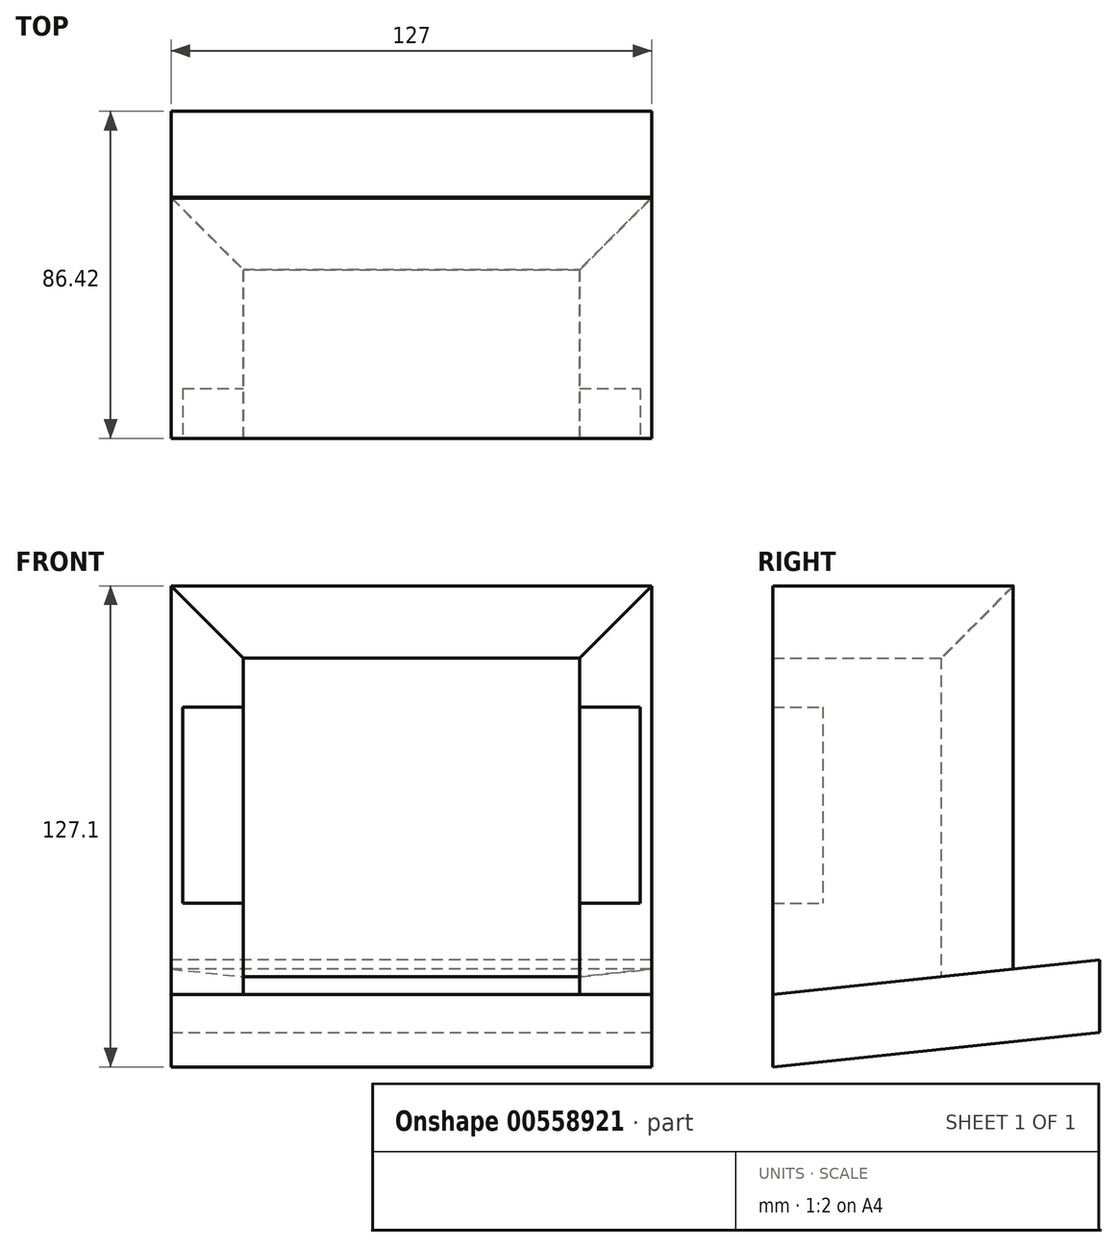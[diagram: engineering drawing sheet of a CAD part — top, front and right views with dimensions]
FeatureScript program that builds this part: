
annotation { "Feature Type Name" : "Feature", "Feature Type Description" : "" }
export const myFeature = defineFeature(function(context is Context, id is Id, definition is map)
    precondition{}
    {
        {
            var Q0;
            Q0=qCreatedBy(makeId("Right.planeOp"),FACE);
            cPlane(context, id + "F0", {"entities" : qUnion([Q0]), "cplaneType" : CPlaneType.OFFSET, "offset" : 63.5 * mm, "oppositeDirection" : true, "width" : 152.4 * mm, "height" : 152.4 * mm});
        }
        {
            var Q0;
            Q0=qCreatedBy(makeId("Right.planeOp"),FACE);
            cPlane(context, id + "F1", {"entities" : qUnion([Q0]), "cplaneType" : CPlaneType.OFFSET, "offset" : 63.5 * mm, "width" : 152.4 * mm, "height" : 152.4 * mm});
        }
        {
            var Q0;
            Q0=qCreatedBy(makeId("Top.planeOp"),FACE);
            cPlane(context, id + "F2", {"entities" : qUnion([Q0]), "cplaneType" : CPlaneType.OFFSET, "offset" : 63.5 * mm, "width" : 152.4 * mm, "height" : 152.4 * mm});
        }
        {
            var Q0;
            Q0=qCreatedBy(makeId("Front.planeOp"),FACE);
            cPlane(context, id + "F3", {"entities" : qUnion([Q0]), "cplaneType" : CPlaneType.OFFSET, "offset" : 63.5 * mm, "width" : 152.4 * mm, "height" : 152.4 * mm});
        }
        {
            var Q0;
            Q0=qCreatedBy(makeId("Front.planeOp"),FACE);
            var sketch = newSketch(context, id + "F4", { "sketchPlane" : qUnion([Q0])});
            skLineSegment(sketch, "E0.bottom", {"start": v(63.5, 63.5) * mm, "end": v(-63.5, 63.5) * mm});
            skLineSegment(sketch, "E0.top", {"start": v(63.5, -39.77) * mm, "end": v(-63.5, -39.77) * mm});
            skLineSegment(sketch, "E0.left", {"start": v(63.5, 63.5) * mm, "end": v(63.5, -39.77) * mm});
            skLineSegment(sketch, "E0.right", {"start": v(-63.5, 63.5) * mm, "end": v(-63.5, -39.77) * mm});
            skSolve(sketch);
        }
        {
            var Q0;
            Q0=makeQuery(id+"F4.imprint","IMPRINT",FACE,{"disambiguationData":[TD([[makeQuery(id+"F4.imprint","IMPRINT",EDGE,{"derivedFrom":sQuery(id+"F4.wireOp",EDGE,"E0.bottom")}),1.0]])]});
            extrude(context, id + "F5", {"entities" : qUnion([Q0]), "depth" : 19.05 * mm, "offsetDistance" : 25.4 * mm});
        }
        {
            var Q0;
            Q0=makeQuery(id+"F5.opExtrude","CAP_EDGE",EDGE,{"disambiguationData":[OSD([sQuery(id+"F4.wireOp",EDGE,"E0.left")])],"isStart":false});
            var Q1;
            Q1=makeQuery(id+"F5.opExtrude","CAP_EDGE",EDGE,{"disambiguationData":[OSD([sQuery(id+"F4.wireOp",EDGE,"E0.bottom")])],"isStart":false});
            var Q2;
            Q2=makeQuery(id+"F5.opExtrude","CAP_EDGE",EDGE,{"disambiguationData":[OSD([sQuery(id+"F4.wireOp",EDGE,"E0.right")])],"isStart":false});
            chamfer(context, id + "F6", {"entities" : qUnion([Q0, Q1, Q2]), "chamferType" : ChamferType.TWO_OFFSETS, "width1" : 19.05 * mm, "oppositeDirection" : false, "width2" : 19.05 * mm, "tangentPropagation" : true});
        }
        {
            var Q0;
            Q0=makeQuery(id+"F5.opExtrude","CAP_EDGE",EDGE,{"disambiguationData":[OSD([sQuery(id+"F4.wireOp",EDGE,"E0.top")])],"isStart":true});
            chamfer(context, id + "F7", {"entities" : qUnion([Q0]), "chamferType" : ChamferType.OFFSET_ANGLE, "width" : 19.05 * mm, "oppositeDirection" : true, "angle" : 6 * degree, "tangentPropagation" : true});
        }
        {
            var Q0;
            Q0=qCreatedBy(id+"F0.planeOp",FACE);
            var sketch = newSketch(context, id + "F8", { "sketchPlane" : qUnion([Q0])});
            skLineSegment(sketch, "E1.bottom", {"start": v(0, 63.5) * mm, "end": v(-63.5, 63.5) * mm});
            skLineSegment(sketch, "E1.top", {"start": v(0, -44.45) * mm, "end": v(-63.5, -44.45) * mm});
            skLineSegment(sketch, "E1.left", {"start": v(0, 63.5) * mm, "end": v(0, -44.45) * mm});
            skLineSegment(sketch, "E1.right", {"start": v(-63.5, 63.5) * mm, "end": v(-63.5, -44.45) * mm});
            skSolve(sketch);
        }
        {
            var Q0;
            Q0 = qSketchRegion(id + "F8", true);
            extrude(context, id + "F9", {"entities" : qUnion([Q0]), "depth" : 19.05 * mm, "offsetDistance" : 25.4 * mm});
        }
        {
            var Q0;
            Q0=makeQuery(id+"F9.opExtrude","SWEPT_EDGE",EDGE,{"disambiguationData":[OSD([sQuery(id+"F8.wireOp",EDGE,"E1.top"),sQuery(id+"F8.wireOp",EDGE,"E1.left")])]});
            chamfer(context, id + "F10", {"entities" : qUnion([Q0]), "chamferType" : ChamferType.OFFSET_ANGLE, "width" : 63.5 * mm, "oppositeDirection" : true, "angle" : 6 * degree, "tangentPropagation" : true});
        }
        {
            var Q0;
            Q0=makeQuery(id+"F9.opExtrude","CAP_EDGE",EDGE,{"disambiguationData":[OSD([sQuery(id+"F8.wireOp",EDGE,"E1.left")])],"isStart":false});
            var Q1;
            Q1=makeQuery(id+"F9.opExtrude","CAP_EDGE",EDGE,{"disambiguationData":[OSD([sQuery(id+"F8.wireOp",EDGE,"E1.bottom")])],"isStart":false});
            chamfer(context, id + "F11", {"entities" : qUnion([Q0, Q1]), "chamferType" : ChamferType.TWO_OFFSETS, "width1" : 19.05 * mm, "oppositeDirection" : true, "width2" : 19.05 * mm, "tangentPropagation" : true});
        }
        {
            var Q0;
            Q0=qCreatedBy(id+"F1.planeOp",FACE);
            var sketch = newSketch(context, id + "F12", { "sketchPlane" : qUnion([Q0])});
            skLineSegment(sketch, "E2.bottom", {"start": v(0, 63.5) * mm, "end": v(-63.5, 63.5) * mm});
            skLineSegment(sketch, "E2.top", {"start": v(0, -44.45) * mm, "end": v(-63.5, -44.45) * mm});
            skLineSegment(sketch, "E2.left", {"start": v(0, 63.5) * mm, "end": v(0, -44.45) * mm});
            skLineSegment(sketch, "E2.right", {"start": v(-63.5, 63.5) * mm, "end": v(-63.5, -44.45) * mm});
            skSolve(sketch);
        }
        {
            var Q0;
            Q0 = qSketchRegion(id + "F12", true);
            extrude(context, id + "F13", {"entities" : qUnion([Q0]), "oppositeDirection" : true, "depth" : 19.05 * mm, "offsetDistance" : 25.4 * mm});
        }
        {
            var Q0;
            Q0=makeQuery(id+"F13.opExtrude","SWEPT_EDGE",EDGE,{"disambiguationData":[OSD([sQuery(id+"F12.wireOp",EDGE,"E2.top"),sQuery(id+"F12.wireOp",EDGE,"E2.left")])]});
            chamfer(context, id + "F14", {"entities" : qUnion([Q0]), "chamferType" : ChamferType.OFFSET_ANGLE, "width" : 63.5 * mm, "oppositeDirection" : false, "angle" : 6 * degree, "tangentPropagation" : true});
        }
        {
            var Q0;
            Q0=makeQuery(id+"F13.opExtrude","CAP_EDGE",EDGE,{"disambiguationData":[OSD([sQuery(id+"F12.wireOp",EDGE,"E2.left")])],"isStart":false});
            var Q1;
            Q1=makeQuery(id+"F13.opExtrude","CAP_EDGE",EDGE,{"disambiguationData":[OSD([sQuery(id+"F12.wireOp",EDGE,"E2.bottom")])],"isStart":false});
            chamfer(context, id + "F15", {"entities" : qUnion([Q0, Q1]), "chamferType" : ChamferType.TWO_OFFSETS, "width1" : 19.05 * mm, "oppositeDirection" : false, "width2" : 19.05 * mm, "tangentPropagation" : true});
        }
        {
            var Q0;
            Q0=qCreatedBy(id+"F2.planeOp",FACE);
            var sketch = newSketch(context, id + "F16", { "sketchPlane" : qUnion([Q0])});
            skLineSegment(sketch, "E3.bottom", {"start": v(-63.5, 0.2) * mm, "end": v(63.5, 0.2) * mm});
            skLineSegment(sketch, "E3.top", {"start": v(-63.5, -63.5) * mm, "end": v(63.5, -63.5) * mm});
            skLineSegment(sketch, "E3.left", {"start": v(-63.5, 0.2) * mm, "end": v(-63.5, -63.5) * mm});
            skLineSegment(sketch, "E3.right", {"start": v(63.5, 0.2) * mm, "end": v(63.5, -63.5) * mm});
            skSolve(sketch);
        }
        {
            var Q0;
            Q0 = qSketchRegion(id + "F16", true);
            extrude(context, id + "F17", {"entities" : qUnion([Q0]), "oppositeDirection" : true, "depth" : 19.05 * mm, "offsetDistance" : 25.4 * mm});
        }
        {
            var Q0;
            Q0=makeQuery(id+"F17.opExtrude","CAP_EDGE",EDGE,{"disambiguationData":[OSD([sQuery(id+"F16.wireOp",EDGE,"E3.bottom")])],"isStart":false});
            var Q1;
            Q1=makeQuery(id+"F17.opExtrude","CAP_EDGE",EDGE,{"disambiguationData":[OSD([sQuery(id+"F16.wireOp",EDGE,"E3.right")])],"isStart":false});
            var Q2;
            Q2=makeQuery(id+"F17.opExtrude","CAP_EDGE",EDGE,{"disambiguationData":[OSD([sQuery(id+"F16.wireOp",EDGE,"E3.left")])],"isStart":false});
            chamfer(context, id + "F18", {"entities" : qUnion([Q0, Q1, Q2]), "chamferType" : ChamferType.TWO_OFFSETS, "width1" : 19.05 * mm, "oppositeDirection" : false, "width2" : 19.05 * mm, "tangentPropagation" : true});
        }
        {
            var Q0;
            Q0=makeQuery(id+"F14.opChamfer","BLEND_EDGE",EDGE,{"blendedFrom":[makeQuery(id+"F13.opExtrude","SWEPT_EDGE",EDGE,{"disambiguationData":[OSD([sQuery(id+"F12.wireOp",EDGE,"E2.top"),sQuery(id+"F12.wireOp",EDGE,"E2.left")])]}),makeQuery(id+"F13.opExtrude","SWEPT_FACE",FACE,{"disambiguationData":[OSD([sQuery(id+"F12.wireOp",EDGE,"E2.right")])]})],"blendedInto":[makeQuery(id+"F13.opExtrude","SWEPT_FACE",FACE,{"disambiguationData":[OSD([sQuery(id+"F12.wireOp",EDGE,"E2.right")])]})]});
            cPlane(context, id + "F19", {"entities" : qUnion([Q0]), "cplaneType" : CPlaneType.LINE_ANGLE, "offset" : 25.4 * mm, "angle" : 96 * degree, "width" : 152.4 * mm, "height" : 152.4 * mm});
        }
        {
            var Q0;
            Q0=qCreatedBy(id+"F19.planeOp",FACE);
            var sketch = newSketch(context, id + "F20", { "sketchPlane" : qUnion([Q0])});
            skLineSegment(sketch, "E4.bottom", {"start": v(63.5, 19.1) * mm, "end": v(-63.5, 19.1) * mm});
            skLineSegment(sketch, "E4.top", {"start": v(63.5, -69.8) * mm, "end": v(-63.5, -69.8) * mm});
            skLineSegment(sketch, "E4.left", {"start": v(63.5, 19.1) * mm, "end": v(63.5, -69.8) * mm});
            skLineSegment(sketch, "E4.right", {"start": v(-63.5, 19.1) * mm, "end": v(-63.5, -69.8) * mm});
            skSolve(sketch);
        }
        {
            var Q0;
            Q0 = qSketchRegion(id + "F20", true);
            extrude(context, id + "F21", {"entities" : qUnion([Q0]), "oppositeDirection" : true, "depth" : 19.05 * mm, "offsetDistance" : 25.4 * mm});
        }
        {
            var Q0;
            Q0=makeQuery(id+"F21.opExtrude","CAP_EDGE",EDGE,{"disambiguationData":[OSD([sQuery(id+"F20.wireOp",EDGE,"E4.top")])],"isStart":true});
            var Q1;
            Q1=makeQuery(id+"F21.opExtrude","CAP_EDGE",EDGE,{"disambiguationData":[OSD([sQuery(id+"F20.wireOp",EDGE,"E4.bottom")])],"isStart":false});
            chamfer(context, id + "F22", {"entities" : qUnion([Q0, Q1]), "chamferType" : ChamferType.OFFSET_ANGLE, "width" : 19.05 * mm, "oppositeDirection" : false, "angle" : 6 * degree, "tangentPropagation" : true});
        }
        {
            var Q0;
            Q0=qCreatedBy(id+"F3.planeOp",FACE);
            var sketch = newSketch(context, id + "F23", { "sketchPlane" : qUnion([Q0])});
            skLineSegment(sketch, "E5.bottom", {"start": v(-60.45, 31.5) * mm, "end": v(60.45, 31.5) * mm});
            skLineSegment(sketch, "E5.top", {"start": v(-60.45, -20.32) * mm, "end": v(60.45, -20.32) * mm});
            skLineSegment(sketch, "E5.left", {"start": v(-60.45, 31.5) * mm, "end": v(-60.45, -20.32) * mm});
            skLineSegment(sketch, "E5.right", {"start": v(60.45, 31.5) * mm, "end": v(60.45, -20.32) * mm});
            skSolve(sketch);
        }
        {
            var Q0;
            Q0 = qSketchRegion(id + "F23", true);
            extrude(context, id + "F24", {"entities" : qUnion([Q0]), "oppositeDirection" : true, "depth" : 13.2 * mm, "offsetDistance" : 25.4 * mm});
        }
        {
            var Q0;
            Q0=makeQuery(id+"F24.opExtrude","SWEPT_BODY",BODY,{"disambiguationData":[OSD([sQuery(id+"F23.wireOp",EDGE,"E5.bottom"),sQuery(id+"F23.wireOp",EDGE,"E5.top"),sQuery(id+"F23.wireOp",EDGE,"E5.left"),sQuery(id+"F23.wireOp",EDGE,"E5.right")])]});
            var Q1;
            Q1=makeQuery(id+"F13.opExtrude","SWEPT_BODY",BODY,{"disambiguationData":[OSD([sQuery(id+"F12.wireOp",EDGE,"E2.bottom"),sQuery(id+"F12.wireOp",EDGE,"E2.top"),sQuery(id+"F12.wireOp",EDGE,"E2.left"),sQuery(id+"F12.wireOp",EDGE,"E2.right")])]});
            var Q2;
            Q2=makeQuery(id+"F9.opExtrude","SWEPT_BODY",BODY,{"disambiguationData":[OSD([sQuery(id+"F8.wireOp",EDGE,"E1.bottom"),sQuery(id+"F8.wireOp",EDGE,"E1.top"),sQuery(id+"F8.wireOp",EDGE,"E1.left"),sQuery(id+"F8.wireOp",EDGE,"E1.right")])]});
            booleanBodies(context, id + "F25", {"operationType" : BooleanOperationType.SUBTRACTION, "tools" : qUnion([Q0]), "targets" : qUnion([Q1, Q2])});
        }
    });
